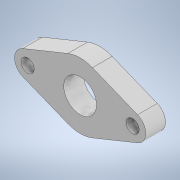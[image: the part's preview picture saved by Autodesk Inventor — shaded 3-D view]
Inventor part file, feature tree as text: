
AUTODESK INVENTOR PART (.ipt)
format: ipt  version: 2022 (Build 260153000, 153)  size: 119,808 bytes
history: native  units: mm
features: other x1, extrude x1, sketch x1
ambient origin geometry x8: Origin, YZ Plane, XZ Plane, XY Plane, X Axis, Y Axis, Z Axis, Center Point
bodies: Body1 (feature_tree)
feature tree (3):
  other  "Sólido1"
  extrude  "Extrusão1"  Depth=10.0mm
  sketch  "Esboço1"  dims[d0=10.0mm d1=10.0mm d2=80.0mm d3=25.0mm d4=40.0mm d5=20.0mm d6=50.0mm d9=20.0mm d10=15.0mm d11=0.0mm]
